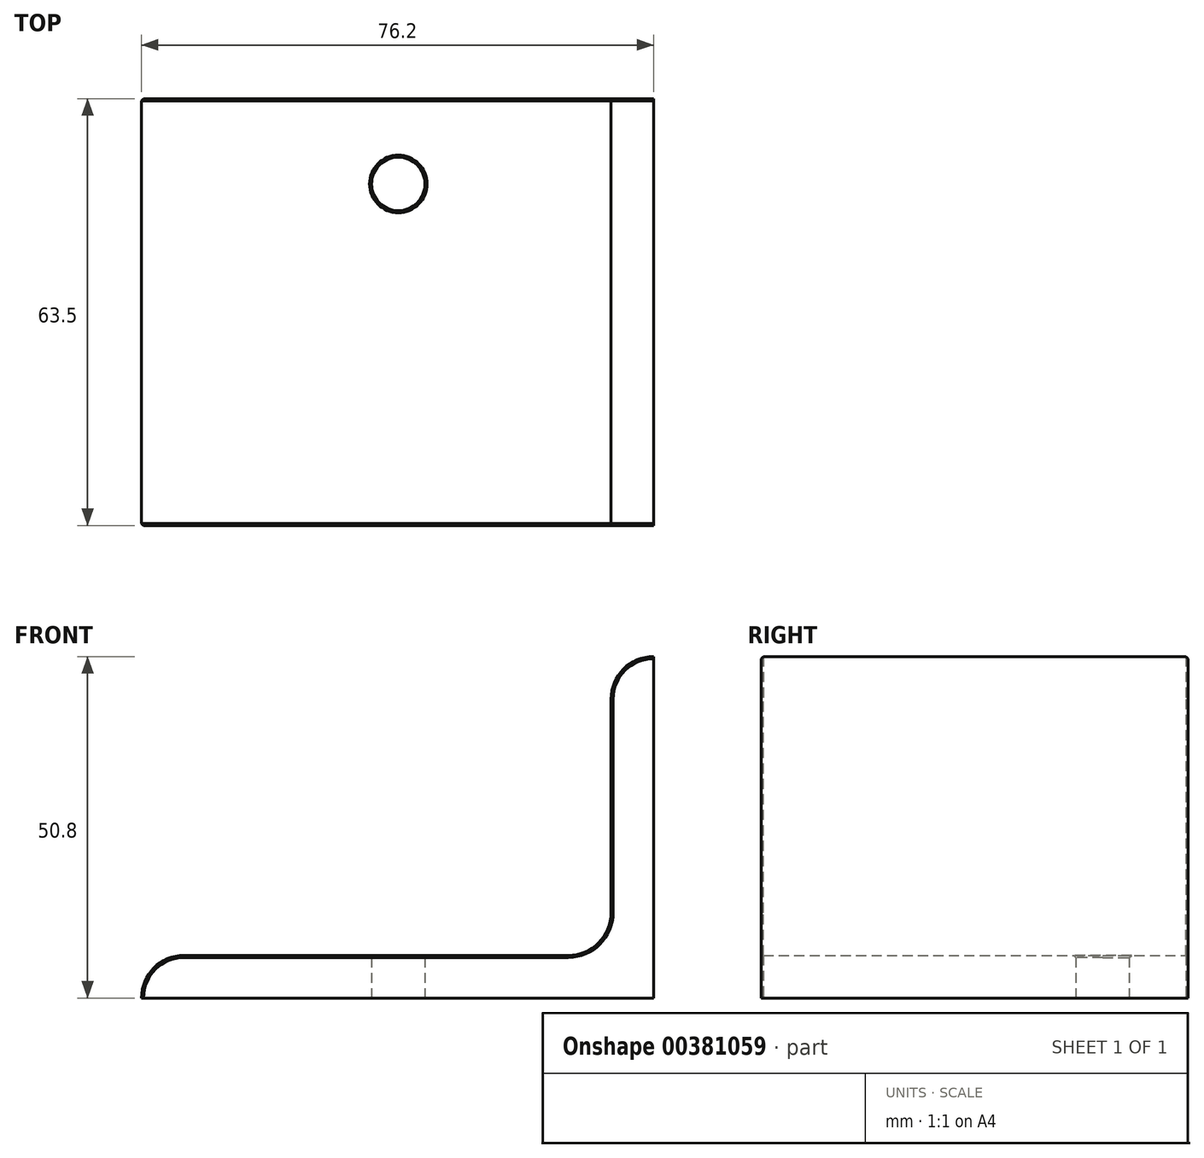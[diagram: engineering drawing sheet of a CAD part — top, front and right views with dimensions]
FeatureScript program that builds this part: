
annotation { "Feature Type Name" : "Feature", "Feature Type Description" : "" }
export const myFeature = defineFeature(function(context is Context, id is Id, definition is map)
    precondition{}
    {
        {
            var Q0;
            Q0=qCreatedBy(makeId("Front.planeOp"),FACE);
            var sketch = newSketch(context, id + "F0", { "sketchPlane" : qUnion([Q0])});
            skLineSegment(sketch, "E0", {"start": v(-0.1, 0) * mm, "end": v(-0.1, 50.8) * mm});
            skLineSegment(sketch, "E1", {"start": v(-0.1, 0) * mm, "end": v(-76.3, 0) * mm});
            skLineSegment(sketch, "E2", {"start": v(-14.84, 88.04) * mm, "end": v(-14.84, 88.04) * mm});
            skLineSegment(sketch, "E3", {"start": v(-91.04, 11.84) * mm, "end": v(-91.04, 11.84) * mm});
            skLineSegment(sketch, "E4", {"start": v(-69.96, 6.35) * mm, "end": v(-12.8, 6.35) * mm});
            skLineSegment(sketch, "E5", {"start": v(-6.46, 12.7) * mm, "end": v(-6.46, 44.45) * mm});
            skPoint(sketch, "E6.visualSharp", {"position": v(-6.46, 6.35) * mm});
            skArc(sketch, "E6.filletArc", {"start": v(-12.8, 6.35) * mm, "mid": v(-8.32, 8.2) * mm, "end": v(-6.46, 12.7) * mm});
            skPoint(sketch, "E7.visualSharp", {"position": v(-6.46, 76.2) * mm});
            skArc(sketch, "E7.filletArc", {"start": v(-0.1, 50.8) * mm, "mid": v(-4.6, 48.94) * mm, "end": v(-6.46, 44.45) * mm});
            skPoint(sketch, "E8.visualSharp", {"position": v(-76.3, 6.35) * mm});
            skArc(sketch, "E8.filletArc", {"start": v(-69.96, 6.35) * mm, "mid": v(-74.45, 4.5) * mm, "end": v(-76.3, 0) * mm});
            skSolve(sketch);
        }
        {
            var Q0;
            Q0=makeQuery(id+"F0.imprint","IMPRINT",FACE,{"disambiguationData":[TD([[makeQuery(id+"F0.imprint","IMPRINT",EDGE,{"derivedFrom":sQuery(id+"F0.wireOp",EDGE,"E0")}),1.0]])]});
            extrude(context, id + "F1", {"entities" : qUnion([Q0]), "depth" : 63.5 * mm, "symmetric" : true});
        }
        {
            var Q0;
            Q0=makeQuery(id+"F1.opExtrude","SWEPT_FACE",FACE,{"disambiguationData":[OSD([sQuery(id+"F0.wireOp",EDGE,"E1")])]});
            var sketch = newSketch(context, id + "F2", { "sketchPlane" : qUnion([Q0])});
            skLineSegment(sketch, "E9", {"start": v(-76.2, -31.75) * mm, "end": v(-34.93, -31.75) * mm});
            skLineSegment(sketch, "E10", {"start": v(-34.93, 0) * mm, "end": v(-34.93, -31.75) * mm});
            skLineSegment(sketch, "E11", {"start": v(-34.93, -31.75) * mm, "end": v(0, -31.75) * mm});
            skLineSegment(sketch, "E12", {"start": v(-34.93, -31.75) * mm, "end": v(-34.93, -19.05) * mm});
            skLineSegment(sketch, "E13", {"start": v(-34.93, -19.05) * mm, "end": v(-38.1, -19.05) * mm});
            skCircle(sketch, "E14", {"center": v(-38.1, -19.05) * mm, "radius": 3.97 * mm});
            skSolve(sketch);
        }
        {
            var Q0;
            {var subQ0=sQuery(id+"F2.wireOp",EDGE,"E12");var subQ1=sQuery(id+"F2.wireOp",EDGE,"E10");var subQ2=makeQuery(id+"F2.imprint","INTERSECT",VERTEX,{"derivedFrom":[subQ1,subQ0]});Q0=makeQuery(id+"F2.imprint","IMPRINT",FACE,{"disambiguationData":[TD([[makeQuery(id+"F2.imprint","IMPRINT",EDGE,{"disambiguationData":[TD([[subQ2,1.0]])],"derivedFrom":subQ1}),-1.0]])]});}
            var Q1;
            {var subQ0=sQuery(id+"F2.wireOp",EDGE,"E12");var subQ1=sQuery(id+"F2.wireOp",EDGE,"E10");var subQ2=makeQuery(id+"F2.imprint","INTERSECT",VERTEX,{"derivedFrom":[subQ1,subQ0]});Q1=makeQuery(id+"F2.imprint","IMPRINT",FACE,{"disambiguationData":[TD([[makeQuery(id+"F2.imprint","IMPRINT",EDGE,{"disambiguationData":[TD([[subQ2,1.0]])],"derivedFrom":subQ1}),1.0]])]});}
            extrude(context, id + "F3", {"entities" : qUnion([Q0, Q1]), "operationType" : NewBodyOperationType.REMOVE, "oppositeDirection" : true, "depth" : 25.4 * mm});
        }
        {
            var Q0;
            Q0=makeQuery(id+"F3.boolean.opBoolean","INTERSECT",EDGE,{"derivedFrom":[makeQuery(id+"F1.opExtrude","SWEPT_FACE",FACE,{"disambiguationData":[OSD([sQuery(id+"F0.wireOp",EDGE,"E4")])]}),makeQuery(id+"F3.opExtrude","SWEPT_FACE",FACE,{"disambiguationData":[OSD([sQuery(id+"F2.wireOp",EDGE,"E14")])]})]});
            var Q1;
            Q1=makeQuery(id+"F1.opExtrude","CAP_EDGE",EDGE,{"disambiguationData":[OSD([sQuery(id+"F0.wireOp",EDGE,"E4")])],"isStart":true});
            var Q2;
            Q2=makeQuery(id+"F1.opExtrude","CAP_EDGE",EDGE,{"disambiguationData":[OSD([sQuery(id+"F0.wireOp",EDGE,"E4")])],"isStart":false});
            var Q3;
            Q3=makeQuery(id+"F3.boolean.opBoolean","COPY",EDGE,{"derivedFrom":makeQuery(id+"F3.opExtrude","CAP_EDGE",EDGE,{"disambiguationData":[OSD([sQuery(id+"F2.wireOp",EDGE,"E14")])],"isStart":true})});
            chamfer(context, id + "F4", {"entities" : qUnion([Q0, Q1, Q2, Q3]), "width" : 0.32 * mm, "tangentPropagation" : true});
        }
    });
